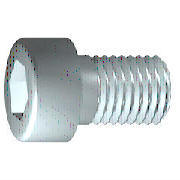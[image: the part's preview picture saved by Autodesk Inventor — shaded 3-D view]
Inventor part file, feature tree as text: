
AUTODESK INVENTOR PART (.ipt)
format: ipt  version: 2020 (Build 240168000, 168)  size: 189,952 bytes
history: native  units: mm (DEFAULTED — no unit token found)
features: sketch x2, extrude x1, plane x1, fillet x1
ambient origin geometry x7: Origin, YZ Plane, XY Plane, X Axis, Y Axis, Z Axis, Center Point
bodies: Solid1 (feature_tree), Body (feature_tree)
feature tree (5):
  extrude  "Slot"  Depth=3.0mm
  plane  "Work Plane1"
  fillet  "Fillet2"  Radius=3.0mm
  sketch  "Sketch1"  dims[d1=18.0mm d2=0.306825mm d3=3.0mm]
  sketch  "Sketch2"  dims[d4=1.3mm d5=60.0deg d6=3.0mm d7=3.0mm d8=2.886751mm d9=5.5mm d10=90.0deg d11=10.0mm d12=0.0mm d13=18.0mm d14=0.0mm d15=0.306725mm d16=0.306725mm d17=0.3mm d19=0.0mm d26=25.0mm d27=45.0deg d28=0.0mm d29=0.0mm d30=0.1mm]
